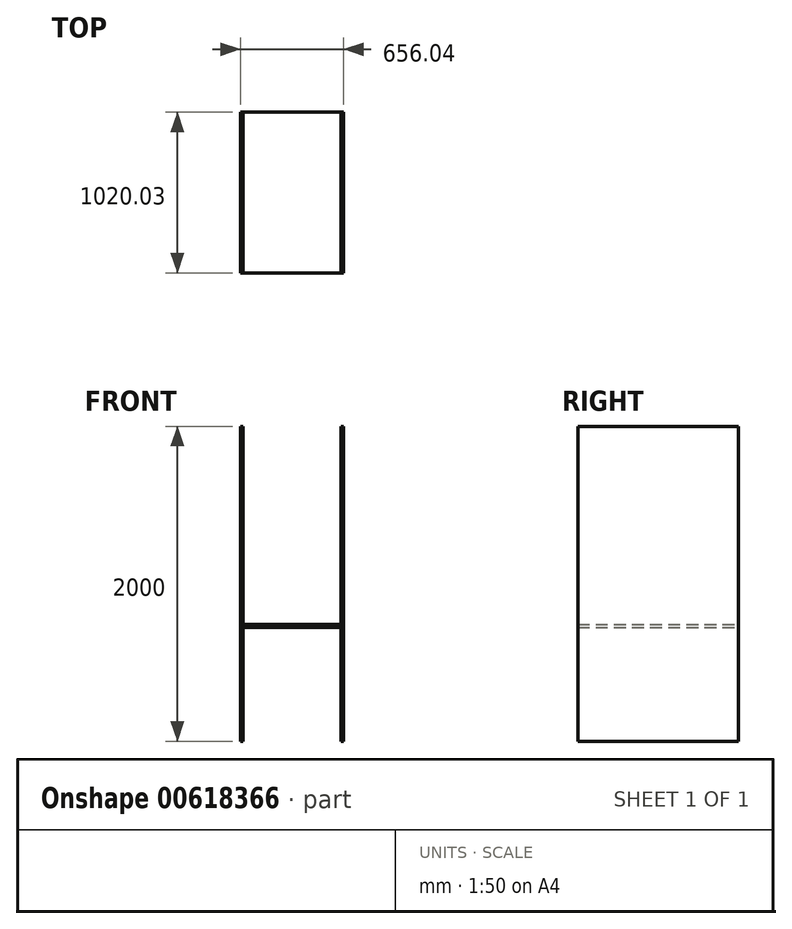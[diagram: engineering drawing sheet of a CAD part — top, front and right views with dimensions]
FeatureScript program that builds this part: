
annotation { "Feature Type Name" : "Feature", "Feature Type Description" : "" }
export const myFeature = defineFeature(function(context is Context, id is Id, definition is map)
    precondition{}
    {
        {
            var Q0;
            Q0=qCreatedBy(makeId("Top.planeOp"),FACE);
            var sketch = newSketch(context, id + "F0", { "sketchPlane" : qUnion([Q0])});
            skLineSegment(sketch, "E0.bottom", {"start": v(-338.52, -532.58) * mm, "end": v(281.48, -532.58) * mm});
            skLineSegment(sketch, "E0.top", {"start": v(-338.52, 487.42) * mm, "end": v(281.48, 487.42) * mm});
            skLineSegment(sketch, "E0.left", {"start": v(-338.52, -532.58) * mm, "end": v(-338.52, 487.42) * mm});
            skLineSegment(sketch, "E0.right", {"start": v(281.48, -532.58) * mm, "end": v(281.48, 487.42) * mm});
            skSolve(sketch);
        }
        {
            var Q0;
            Q0=makeQuery(id+"F0.imprint","IMPRINT",FACE,{"disambiguationData":[TD([[makeQuery(id+"F0.imprint","IMPRINT",EDGE,{"derivedFrom":sQuery(id+"F0.wireOp",EDGE,"E0.bottom")}),1.0]])]});
            extrude(context, id + "F1", {"entities" : qUnion([Q0]), "depth" : 18.05 * mm, "offsetDistance" : 25 * mm});
        }
        {
            var Q0;
            Q0=qCreatedBy(makeId("Right.planeOp"),FACE);
            var sketch = newSketch(context, id + "F2", { "sketchPlane" : qUnion([Q0])});
            skLineSegment(sketch, "E1.bottom", {"start": v(-474.25, 1275.46) * mm, "end": v(545.75, 1275.46) * mm});
            skLineSegment(sketch, "E1.top", {"start": v(-474.25, -724.54) * mm, "end": v(545.75, -724.54) * mm});
            skLineSegment(sketch, "E1.left", {"start": v(-474.25, 1275.46) * mm, "end": v(-474.25, -724.54) * mm});
            skLineSegment(sketch, "E1.right", {"start": v(545.75, 1275.46) * mm, "end": v(545.75, -724.54) * mm});
            skSolve(sketch);
        }
        {
            var Q0;
            Q0=makeQuery(id+"F2.imprint","IMPRINT",FACE,{"disambiguationData":[TD([[makeQuery(id+"F2.imprint","IMPRINT",EDGE,{"derivedFrom":sQuery(id+"F2.wireOp",EDGE,"E1.bottom")}),-1.0]])]});
            extrude(context, id + "F3", {"entities" : qUnion([Q0]), "depth" : 18 * mm, "offsetDistance" : 25 * mm});
        }
        {
            var Q0;
            Q0=makeQuery(id+"F3.opExtrude","SWEPT_BODY",BODY,{"disambiguationData":[OSD([sQuery(id+"F2.wireOp",EDGE,"E1.bottom"),sQuery(id+"F2.wireOp",EDGE,"E1.top"),sQuery(id+"F2.wireOp",EDGE,"E1.left"),sQuery(id+"F2.wireOp",EDGE,"E1.right")])]});
            transform(context, id + "F4", {"entities" : qUnion([Q0]), "transformType" : TransformType.TRANSLATION_3D, "dx" : 281.5 * mm, "dy" : -58.3 * mm, "dz" : 0 * mm, "makeCopy" : false});
        }
        {
            var Q0;
            Q0=makeQuery(id+"F3.opExtrude","SWEPT_BODY",BODY,{"disambiguationData":[OSD([sQuery(id+"F2.wireOp",EDGE,"E1.bottom"),sQuery(id+"F2.wireOp",EDGE,"E1.top"),sQuery(id+"F2.wireOp",EDGE,"E1.left"),sQuery(id+"F2.wireOp",EDGE,"E1.right")])]});
            var Q1;
            Q1=makeQuery(id+"F1.opExtrude","SWEPT_FACE",FACE,{"disambiguationData":[OSD([sQuery(id+"F0.wireOp",EDGE,"E0.left")])]});
            mirror(context, id + "F5", {"entities" : qUnion([Q0]), "mirrorPlane" : qUnion([Q1])});
        }
        {
            var Q0;
            Q0=makeQuery(id+"F5.opPattern","COPY",BODY,{"derivedFrom":makeQuery(id+"F3.opExtrude","SWEPT_BODY",BODY,{"disambiguationData":[OSD([sQuery(id+"F2.wireOp",EDGE,"E1.bottom"),sQuery(id+"F2.wireOp",EDGE,"E1.top"),sQuery(id+"F2.wireOp",EDGE,"E1.left"),sQuery(id+"F2.wireOp",EDGE,"E1.right")])]}),"instanceName":"1"});
            transform(context, id + "F6", {"entities" : qUnion([Q0]), "transformType" : TransformType.TRANSLATION_3D, "dx" : 620 * mm, "dy" : 0 * mm, "dz" : 0 * mm, "makeCopy" : false});
        }
    });
